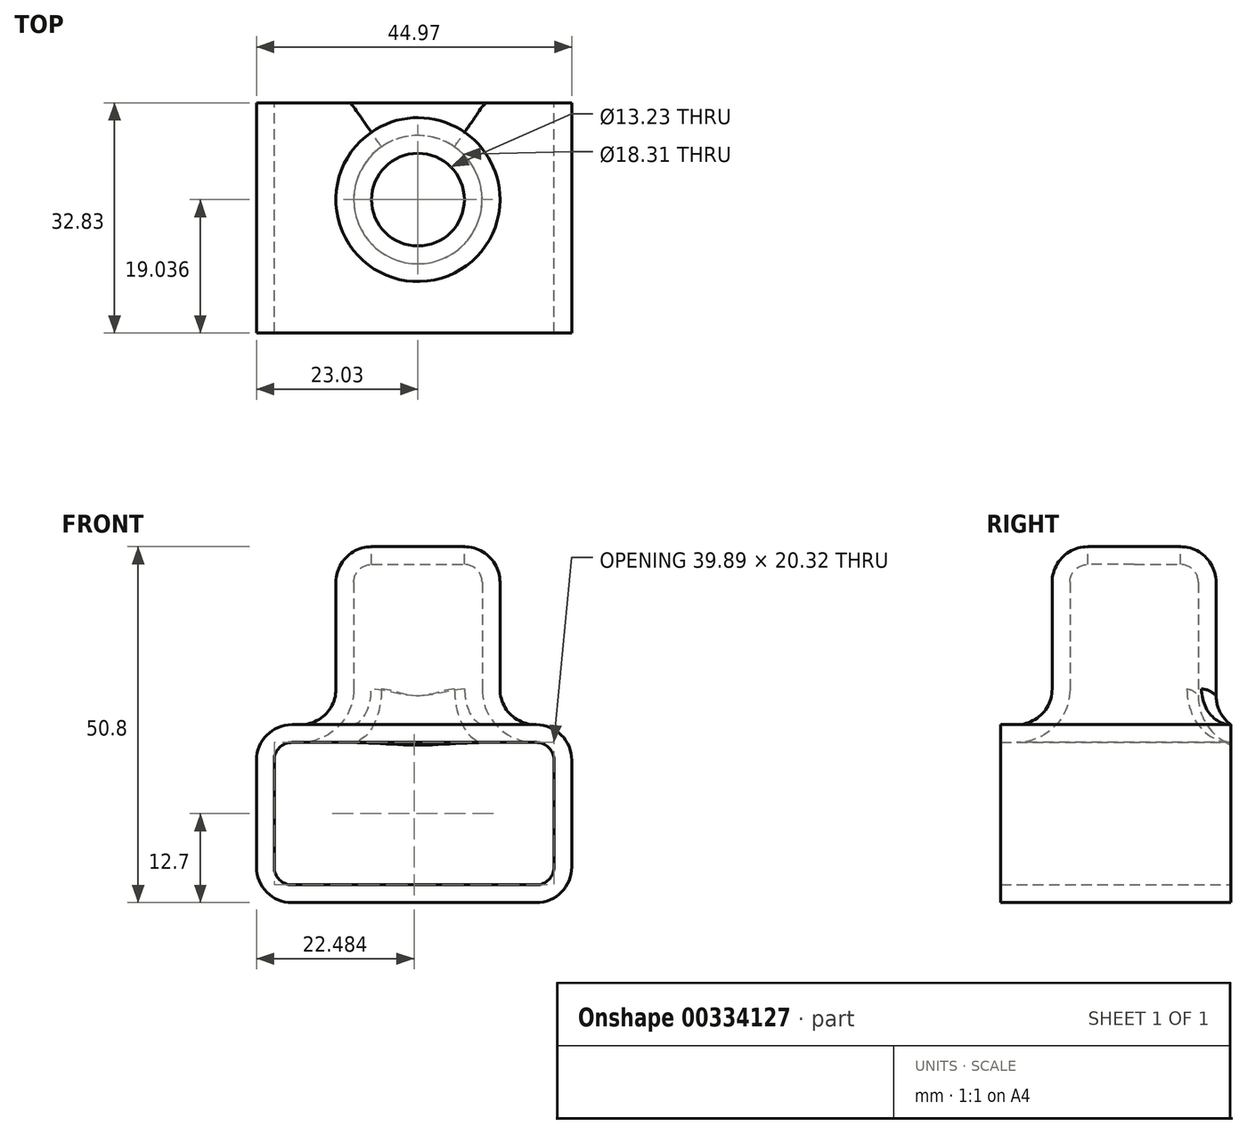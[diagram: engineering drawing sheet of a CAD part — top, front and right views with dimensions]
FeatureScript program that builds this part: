
annotation { "Feature Type Name" : "Feature", "Feature Type Description" : "" }
export const myFeature = defineFeature(function(context is Context, id is Id, definition is map)
    precondition{}
    {
        {
            var Q0;
            Q0=qCreatedBy(makeId("Top.planeOp"),FACE);
            var sketch = newSketch(context, id + "F0", { "sketchPlane" : qUnion([Q0])});
            skLineSegment(sketch, "E0.bottom", {"start": v(-44.97, -32.83) * mm, "end": v(0, -32.83) * mm});
            skLineSegment(sketch, "E0.top", {"start": v(-44.97, 0) * mm, "end": v(0, 0) * mm});
            skLineSegment(sketch, "E0.left", {"start": v(-44.97, -32.83) * mm, "end": v(-44.97, 0) * mm});
            skLineSegment(sketch, "E0.right", {"start": v(0, -32.83) * mm, "end": v(0, 0) * mm});
            skSolve(sketch);
        }
        {
            var Q0;
            Q0=makeQuery(id+"F0.imprint","IMPRINT",FACE,{"disambiguationData":[TD([[makeQuery(id+"F0.imprint","IMPRINT",EDGE,{"derivedFrom":sQuery(id+"F0.wireOp",EDGE,"E0.bottom")}),1.0]])]});
            extrude(context, id + "F1", {"entities" : qUnion([Q0]), "depth" : 25.4 * mm});
        }
        {
            var Q0;
            Q0=makeQuery(id+"F1.opExtrude","CAP_FACE",FACE,{"disambiguationData":[OSD([sQuery(id+"F0.wireOp",EDGE,"E0.bottom"),sQuery(id+"F0.wireOp",EDGE,"E0.top"),sQuery(id+"F0.wireOp",EDGE,"E0.left"),sQuery(id+"F0.wireOp",EDGE,"E0.right")])],"isStart":false});
            var sketch = newSketch(context, id + "F2", { "sketchPlane" : qUnion([Q0])});
            skCircle(sketch, "E1", {"center": v(-21.94, -13.8) * mm, "radius": 11.7 * mm});
            skSolve(sketch);
        }
        {
            var Q0;
            Q0 = qSketchRegion(id + "F2", true);
            extrude(context, id + "F3", {"entities" : qUnion([Q0]), "operationType" : NewBodyOperationType.ADD, "depth" : 25.4 * mm});
        }
        {
            var Q0;
            Q0=makeQuery(id+"F3.opExtrude","SWEPT_FACE",FACE,{"disambiguationData":[OSD([sQuery(id+"F2.wireOp",EDGE,"E1")])]});
            var Q1;
            Q1=makeQuery(id+"F1.opExtrude","CAP_EDGE",EDGE,{"disambiguationData":[OSD([sQuery(id+"F0.wireOp",EDGE,"E0.left")])],"isStart":false});
            var Q2;
            Q2=makeQuery(id+"F1.opExtrude","CAP_EDGE",EDGE,{"disambiguationData":[OSD([sQuery(id+"F0.wireOp",EDGE,"E0.right")])],"isStart":false});
            var Q3;
            Q3=makeQuery(id+"F1.opExtrude","CAP_EDGE",EDGE,{"disambiguationData":[OSD([sQuery(id+"F0.wireOp",EDGE,"E0.left")])],"isStart":true});
            var Q4;
            Q4=makeQuery(id+"F1.opExtrude","CAP_EDGE",EDGE,{"disambiguationData":[OSD([sQuery(id+"F0.wireOp",EDGE,"E0.right")])],"isStart":true});
            fillet(context, id + "F4", {"entities" : qUnion([Q0, Q1, Q2, Q3, Q4]), "radius" : 5.08 * mm, "tangentPropagation" : true, "allowEdgeOverflow" : false});
        }
        {
            var Q0;
            Q0=makeQuery(id+"F3.opExtrude","CAP_FACE",FACE,{"disambiguationData":[OSD([sQuery(id+"F2.wireOp",EDGE,"E1")])],"isStart":false});
            var Q1;
            Q1=makeQuery(id+"F1.opExtrude","SWEPT_FACE",FACE,{"disambiguationData":[OSD([sQuery(id+"F0.wireOp",EDGE,"E0.top")])]});
            var Q2;
            Q2=makeQuery(id+"F1.opExtrude","SWEPT_FACE",FACE,{"disambiguationData":[OSD([sQuery(id+"F0.wireOp",EDGE,"E0.bottom")])]});
            shell(context, id + "F5", {"entities" : qUnion([Q0, Q1, Q2]), "thickness" : 2.54 * mm});
        }
    });
